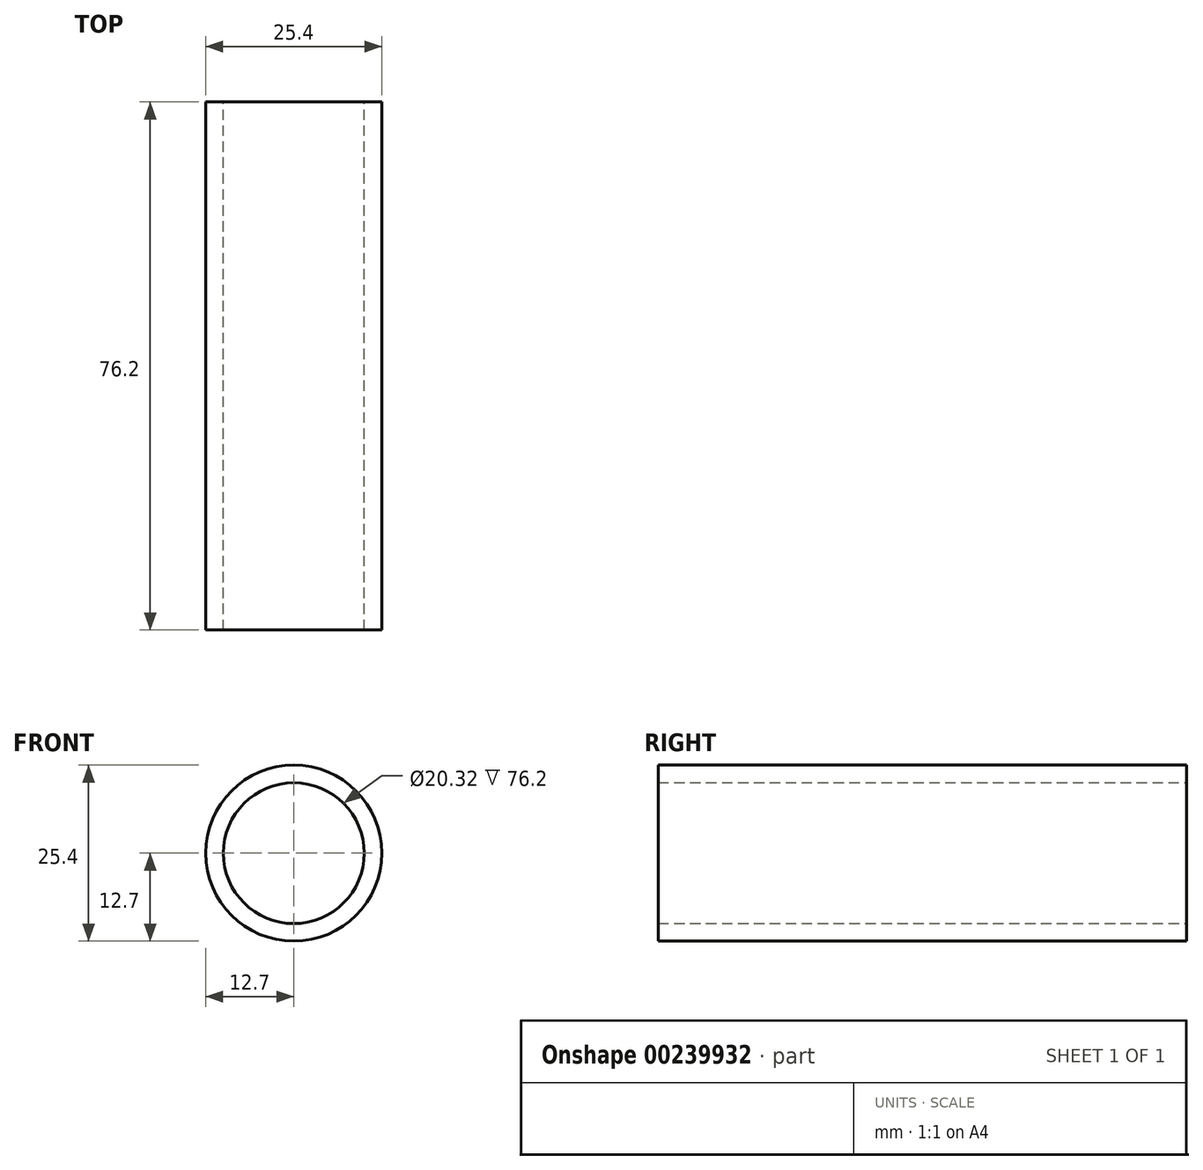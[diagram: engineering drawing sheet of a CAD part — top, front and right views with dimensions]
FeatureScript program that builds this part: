
annotation { "Feature Type Name" : "Feature", "Feature Type Description" : "" }
export const myFeature = defineFeature(function(context is Context, id is Id, definition is map)
    precondition{}
    {
        {
            var Q0;
            Q0=qCreatedBy(makeId("Front.planeOp"),FACE);
            var sketch = newSketch(context, id + "F0", { "sketchPlane" : qUnion([Q0])});
            skCircle(sketch, "E0", {"center": v(0, 0) * mm, "radius": 12.7 * mm});
            skCircle(sketch, "E1", {"center": v(0, 0) * mm, "radius": 10.16 * mm});
            skSolve(sketch);
        }
        {
            var Q0;
            Q0 = qSketchRegion(id + "F0", true);
            extrude(context, id + "F1", {"entities" : qUnion([Q0]), "depth" : 76.2 * mm});
        }
    });
